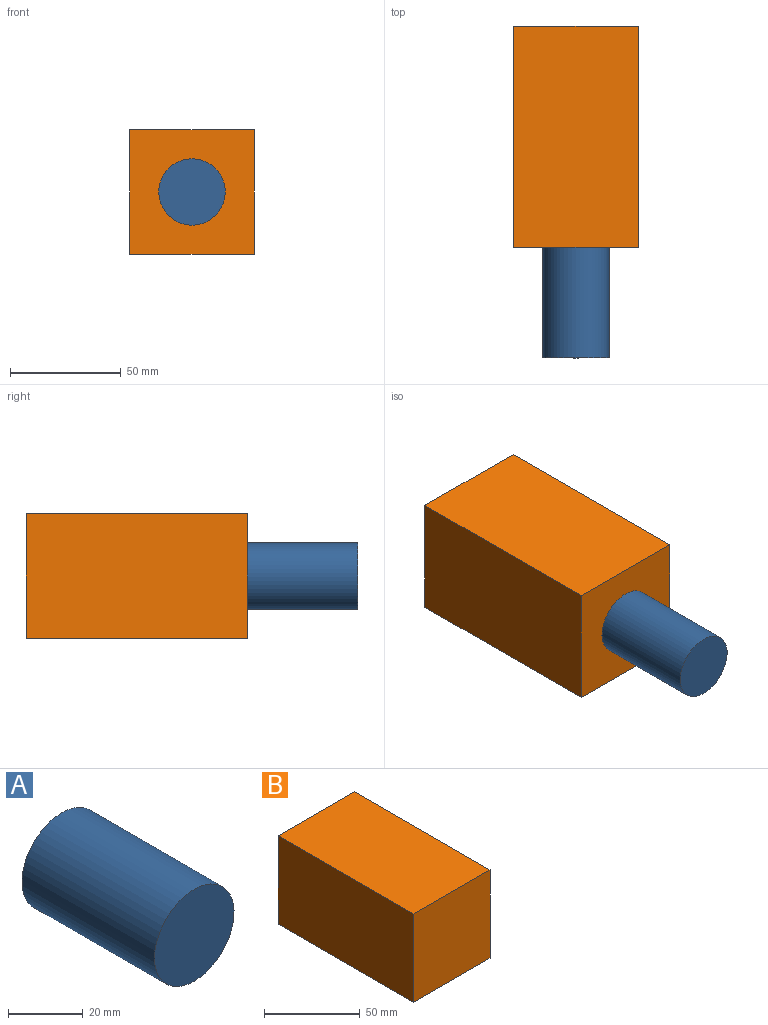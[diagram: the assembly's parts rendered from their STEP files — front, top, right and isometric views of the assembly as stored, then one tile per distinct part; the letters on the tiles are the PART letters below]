
ASSEMBLY  parts=2 mates=1
PART A: 3 faces, bbox 30x50x30 mm
  f0: cylinder r=15mm len=50mm, axis (0,-1,0), area 4712.4mm2, adj f1,f2
  f1: plane 30x30mm, normal (0,1,0), area 706.9mm2, adj f0
  f2: plane 30x30mm, normal (0,-1,0), area 706.9mm2, adj f0
PART B: 6 faces, bbox 56.4x100x56.4 mm
  f0: plane 100x56.4mm, normal (1,0,0), area 5640mm2, adj f1,f3,f4,f5
  f1: plane 100x56.4mm, normal (0,0,1), area 5640mm2, adj f0,f2,f4,f5
  f2: plane 100x56.4mm, normal (-1,0,0), area 5640mm2, adj f1,f3,f4,f5
  f3: plane 100x56.4mm, normal (0,0,-1), area 5640mm2, adj f0,f2,f4,f5
  f4: plane 56.4x56.4mm, normal (0,1,0), area 3181mm2, adj f0,f1,f2,f3
  f5: plane 56.4x56.4mm, normal (0,-1,0), area 3181mm2, adj f0,f1,f2,f3
PLACE A rot(axis=(1,0,0),180deg) t=(-19.94,-43.06,27.68)mm
PLACE B t=(-19.94,-43.06,27.68)mm
MATE fastened A.f0 <-> B.f5  axis (0,1,0) through (-19.94,-43.06,27.68)mm
